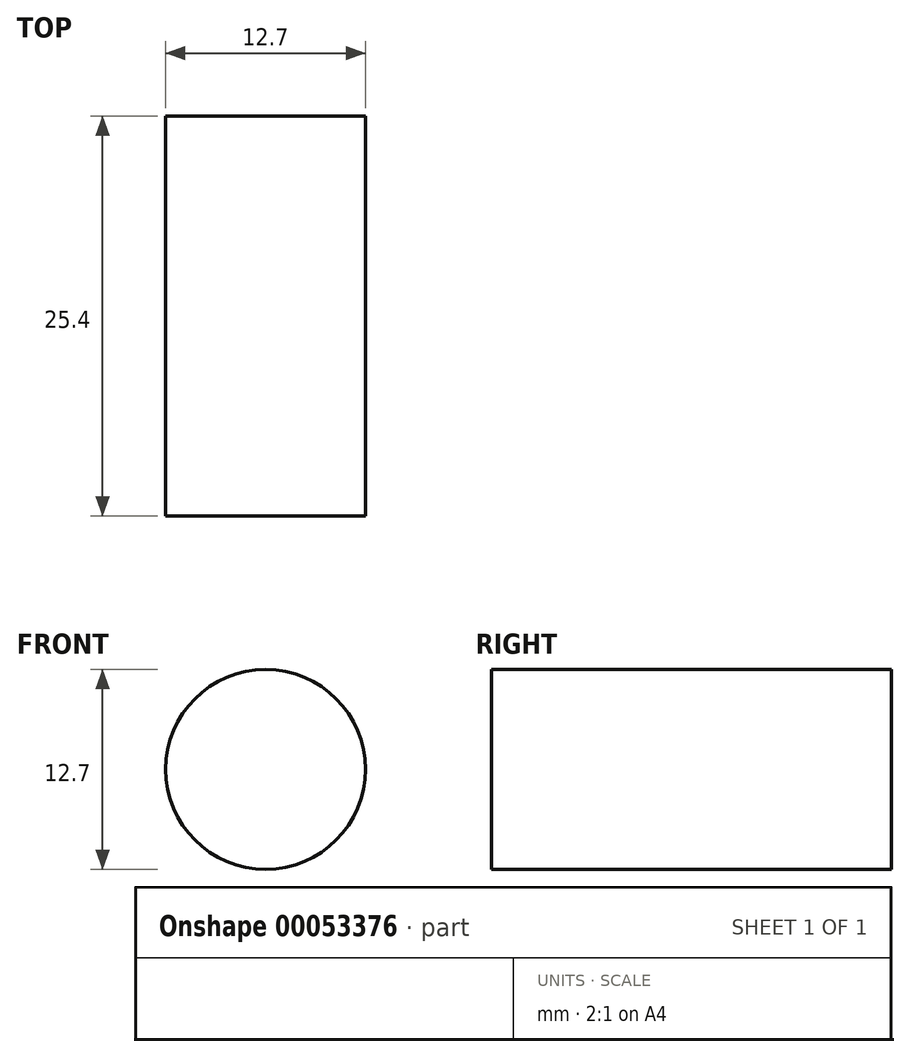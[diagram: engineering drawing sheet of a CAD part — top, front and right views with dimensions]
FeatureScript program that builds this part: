
annotation { "Feature Type Name" : "Feature", "Feature Type Description" : "" }
export const myFeature = defineFeature(function(context is Context, id is Id, definition is map)
    precondition{}
    {
        {
            var Q0;
            Q0=qCreatedBy(makeId("Front.planeOp"),FACE);
            var sketch = newSketch(context, id + "F0", { "sketchPlane" : qUnion([Q0])});
            skCircle(sketch, "E0", {"center": v(-36.19, 16.3) * mm, "radius": 6.35 * mm});
            skSolve(sketch);
        }
        {
            var Q0;
            Q0=makeQuery(id+"F0.imprint","IMPRINT",FACE,{"disambiguationData":[TD([[makeQuery(id+"F0.imprint","IMPRINT",EDGE,{"derivedFrom":sQuery(id+"F0.wireOp",EDGE,"E0")}),1.0]])]});
            extrude(context, id + "F1", {"entities" : qUnion([Q0]), "depth" : 25.4 * mm});
        }
    });
